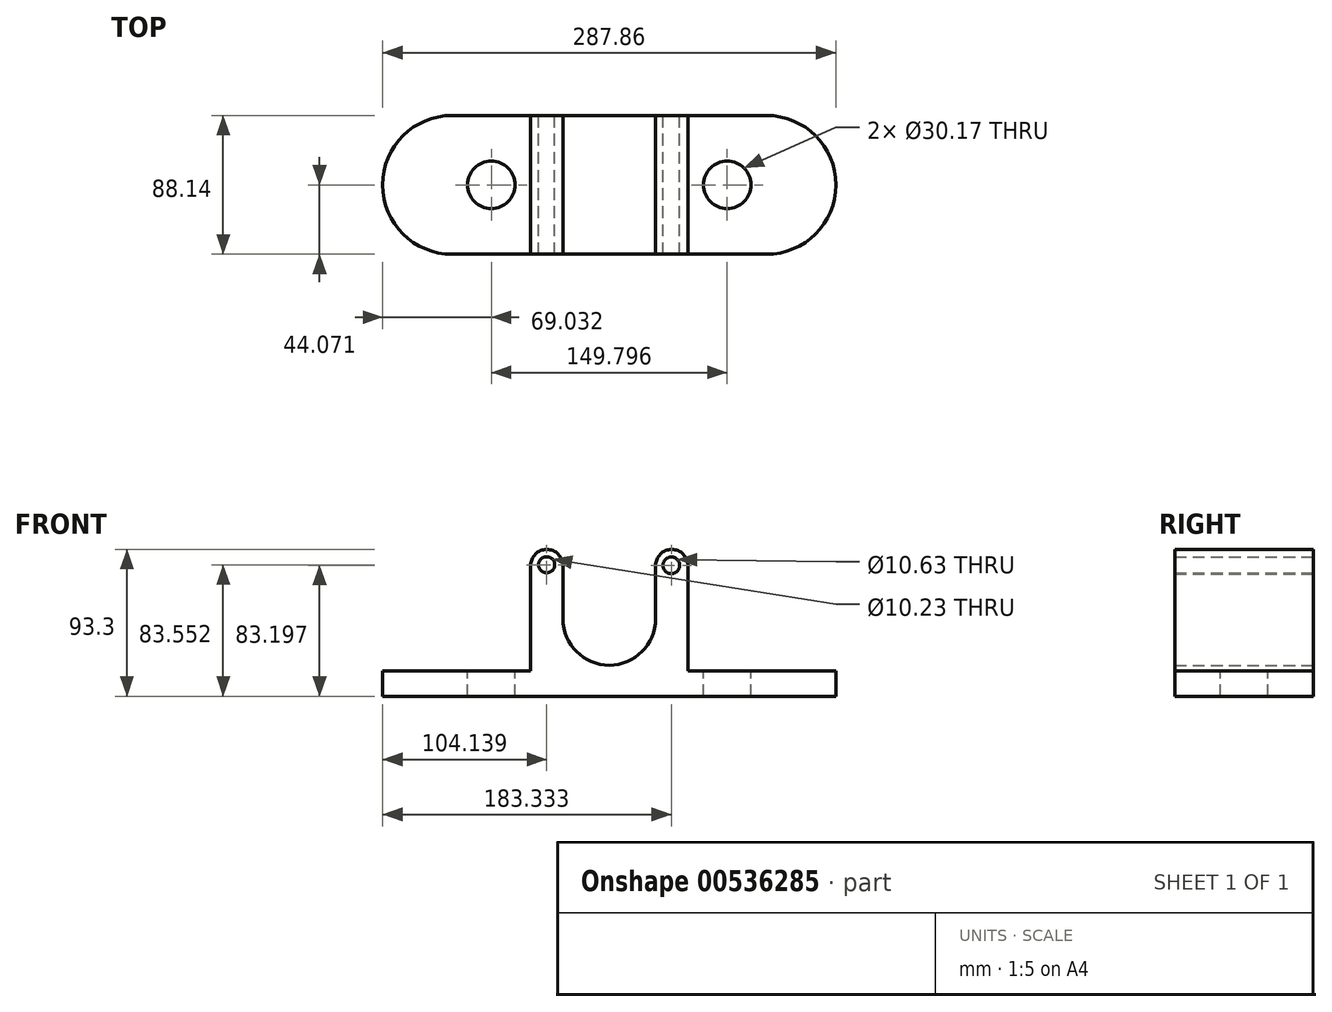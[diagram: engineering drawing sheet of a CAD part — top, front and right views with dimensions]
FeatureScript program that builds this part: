
annotation { "Feature Type Name" : "Feature", "Feature Type Description" : "" }
export const myFeature = defineFeature(function(context is Context, id is Id, definition is map)
    precondition{}
    {
        {
            var Q0;
            Q0=qCreatedBy(makeId("Front.planeOp"),FACE);
            var sketch = newSketch(context, id + "F0", { "sketchPlane" : qUnion([Q0])});
            skLineSegment(sketch, "E0.top", {"start": v(-99.86, -8.07) * mm, "end": v(99.86, -8.07) * mm});
            skLineSegment(sketch, "E0.left", {"start": v(-99.86, 8.07) * mm, "end": v(-99.86, -8.07) * mm});
            skLineSegment(sketch, "E0.right", {"start": v(99.86, 8.07) * mm, "end": v(99.86, -8.07) * mm});
            skPoint(sketch, "E0.middle", {"position": v(0, 0) * mm});
            skLineSegment(sketch, "E1", {"start": v(-99.86, 8.07) * mm, "end": v(-49.93, 8.07) * mm});
            skLineSegment(sketch, "E2", {"start": v(99.86, 8.07) * mm, "end": v(49.93, 8.07) * mm});
            skLineSegment(sketch, "E3", {"start": v(-49.93, 8.07) * mm, "end": v(-49.93, 74.97) * mm});
            skLineSegment(sketch, "E4", {"start": v(-29.42, 74.97) * mm, "end": v(-29.42, 41.08) * mm});
            skLineSegment(sketch, "E5.MirrorCS", {"start": v(49.93, 8.07) * mm, "end": v(49.93, 74.97) * mm});
            skLineSegment(sketch, "E6.MirrorCS", {"start": v(29.42, 74.97) * mm, "end": v(29.42, 41.08) * mm});
            skArc(sketch, "E7", {"start": v(-29.42, 41.08) * mm, "mid": v(0, 11.65) * mm, "end": v(29.42, 41.08) * mm});
            skArc(sketch, "E8", {"start": v(-29.42, 74.97) * mm, "mid": v(-39.68, 85.22) * mm, "end": v(-49.93, 74.97) * mm});
            skArc(sketch, "E9", {"start": v(49.93, 74.97) * mm, "mid": v(39.68, 85.22) * mm, "end": v(29.42, 74.97) * mm});
            skSolve(sketch);
        }
        {
            var Q0;
            Q0=makeQuery(id+"F0.imprint","IMPRINT",FACE,{"disambiguationData":[TD([[makeQuery(id+"F0.imprint","IMPRINT",EDGE,{"derivedFrom":sQuery(id+"F0.wireOp",EDGE,"E0.top")}),1.0]])]});
            var sketch = newSketch(context, id + "F1", { "sketchPlane" : qUnion([Q0])});
            skCircle(sketch, "E10", {"center": v(-39.8, 75.47) * mm, "radius": 5.11 * mm});
            skCircle(sketch, "E11", {"center": v(39.4, 75.12) * mm, "radius": 5.31 * mm});
            skSolve(sketch);
        }
        {
            var Q0;
            Q0=makeQuery(id+"F1.imprint","IMPRINT",FACE,{"disambiguationData":[TD([[makeQuery(id+"F1.imprint","IMPRINT",EDGE,{"derivedFrom":sQuery(id+"F1.wireOp",EDGE,"E10")}),-1.0]])]});
            extrude(context, id + "F2", {"entities" : qUnion([Q0]), "depth" : 88.14 * mm, "offsetDistance" : 25.4 * mm});
        }
        {
            var Q0;
            Q0=makeQuery(id+"F2.opExtrude","SWEPT_FACE",FACE,{"disambiguationData":[OSD([sQuery(id+"F0.wireOp",EDGE,"E1")])]});
            var sketch = newSketch(context, id + "F3", { "sketchPlane" : qUnion([Q0])});
            skCircle(sketch, "E12", {"center": v(-74.9, -44.07) * mm, "radius": 15.08 * mm});
            skPoint(sketch, "E12.centerSnap0", {"position": v(-74.9, 0) * mm});
            skPoint(sketch, "E12.centerSnap1", {"position": v(-99.86, -44.07) * mm});
            skSolve(sketch);
        }
        {
            var Q0;
            Q0=makeQuery(id+"F2.opExtrude","SWEPT_FACE",FACE,{"disambiguationData":[OSD([sQuery(id+"F0.wireOp",EDGE,"E2")])]});
            var sketch = newSketch(context, id + "F4", { "sketchPlane" : qUnion([Q0])});
            skCircle(sketch, "E13", {"center": v(74.9, -44.07) * mm, "radius": 15.08 * mm});
            skPoint(sketch, "E13.centerSnap0", {"position": v(99.86, -44.07) * mm});
            skPoint(sketch, "E13.centerSnap1", {"position": v(74.9, 0) * mm});
            skSolve(sketch);
        }
        {
            var Q0;
            Q0=makeQuery(id+"F3.imprint","IMPRINT",FACE,{"disambiguationData":[TD([[makeQuery(id+"F3.imprint","IMPRINT",EDGE,{"derivedFrom":sQuery(id+"F3.wireOp",EDGE,"E12")}),1.0]])]});
            extrude(context, id + "F5", {"entities" : qUnion([Q0]), "operationType" : NewBodyOperationType.REMOVE, "oppositeDirection" : true, "depth" : 25.4 * mm, "offsetDistance" : 25.4 * mm});
        }
        {
            var Q0;
            Q0=makeQuery(id+"F4.imprint","IMPRINT",FACE,{"disambiguationData":[TD([[makeQuery(id+"F4.imprint","IMPRINT",EDGE,{"derivedFrom":sQuery(id+"F4.wireOp",EDGE,"E13")}),1.0]])]});
            extrude(context, id + "F6", {"entities" : qUnion([Q0]), "operationType" : NewBodyOperationType.REMOVE, "oppositeDirection" : true, "depth" : 25.4 * mm, "offsetDistance" : 25.4 * mm});
        }
        {
            var Q0;
            Q0=makeQuery(id+"F2.opExtrude","SWEPT_FACE",FACE,{"disambiguationData":[OSD([sQuery(id+"F0.wireOp",EDGE,"E2")])]});
            var sketch = newSketch(context, id + "F7", { "sketchPlane" : qUnion([Q0])});
            skArc(sketch, "E14", {"start": v(99.86, -88.14) * mm, "mid": v(143.93, -44.07) * mm, "end": v(99.86, 0) * mm});
            skSolve(sketch);
        }
        {
            var Q0;
            Q0=makeQuery(id+"F7.imprint","IMPRINT",FACE,{"disambiguationData":[TD([[makeQuery(id+"F7.imprint","IMPRINT",EDGE,{"derivedFrom":sQuery(id+"F7.wireOp",EDGE,"E14")}),1.0]])]});
            extrude(context, id + "F8", {"entities" : qUnion([Q0]), "operationType" : NewBodyOperationType.ADD, "oppositeDirection" : true, "depth" : 16.15 * mm, "offsetDistance" : 25.4 * mm});
        }
        {
            var Q0;
            Q0=makeQuery(id+"F2.opExtrude","SWEPT_FACE",FACE,{"disambiguationData":[OSD([sQuery(id+"F0.wireOp",EDGE,"E1")])]});
            var sketch = newSketch(context, id + "F9", { "sketchPlane" : qUnion([Q0])});
            skArc(sketch, "E15", {"start": v(-99.86, 0) * mm, "mid": v(-143.93, -44.07) * mm, "end": v(-99.86, -88.14) * mm});
            skSolve(sketch);
        }
        {
            var Q0;
            Q0=makeQuery(id+"F9.imprint","IMPRINT",FACE,{"disambiguationData":[TD([[makeQuery(id+"F9.imprint","IMPRINT",EDGE,{"derivedFrom":sQuery(id+"F9.wireOp",EDGE,"E15")}),1.0]])]});
            extrude(context, id + "F10", {"entities" : qUnion([Q0]), "operationType" : NewBodyOperationType.ADD, "oppositeDirection" : true, "depth" : 16.15 * mm, "offsetDistance" : 25.4 * mm});
        }
    });
